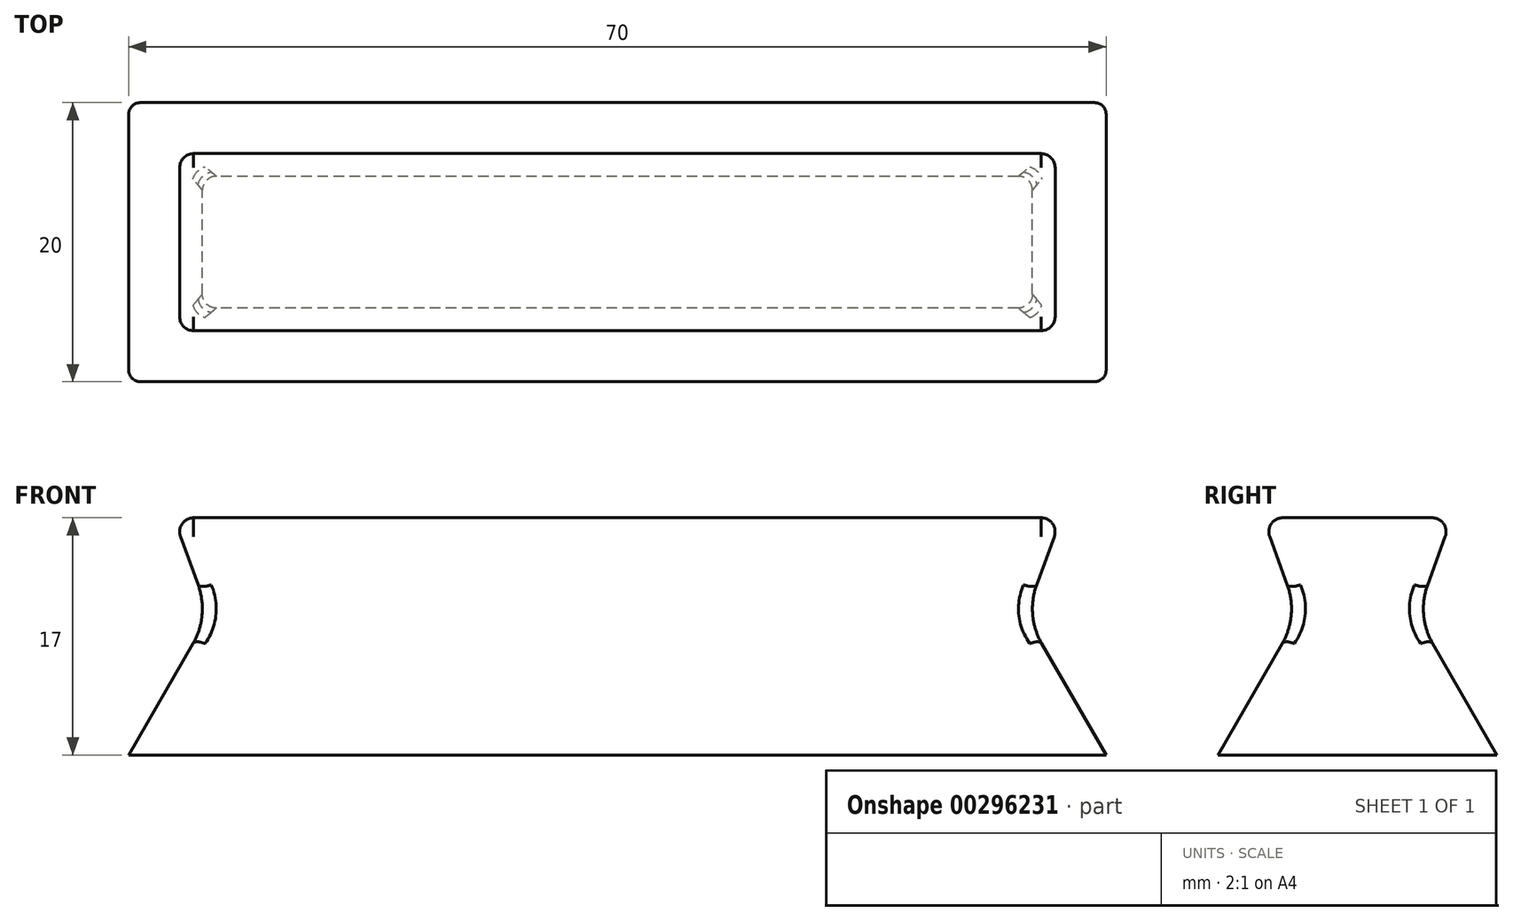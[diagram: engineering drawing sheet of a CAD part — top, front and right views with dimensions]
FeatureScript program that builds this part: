
annotation { "Feature Type Name" : "Feature", "Feature Type Description" : "" }
export const myFeature = defineFeature(function(context is Context, id is Id, definition is map)
    precondition{}
    {
        {
            var Q0;
            Q0=qCreatedBy(makeId("Top.planeOp"),FACE);
            var sketch = newSketch(context, id + "F0", { "sketchPlane" : qUnion([Q0])});
            skLineSegment(sketch, "E0.bottom", {"start": v(-35, 10) * mm, "end": v(35, 10) * mm});
            skLineSegment(sketch, "E0.top", {"start": v(-35, -10) * mm, "end": v(35, -10) * mm});
            skLineSegment(sketch, "E0.left", {"start": v(-35, 10) * mm, "end": v(-35, -10) * mm});
            skLineSegment(sketch, "E0.right", {"start": v(35, 10) * mm, "end": v(35, -10) * mm});
            skPoint(sketch, "E0.middle", {"position": v(0, 0) * mm});
            skSolve(sketch);
        }
        {
            var Q0;
            Q0=makeQuery(id+"F0.imprint","IMPRINT",FACE,{"disambiguationData":[TD([[makeQuery(id+"F0.imprint","IMPRINT",EDGE,{"derivedFrom":sQuery(id+"F0.wireOp",EDGE,"E0.bottom")}),-1.0]])]});
            extrude(context, id + "F1", {"entities" : qUnion([Q0]), "depth" : 10 * mm, "hasDraft" : true, "draftAngle" : 30 * degree, "draftPullDirection" : true});
        }
        {
            var Q0;
            Q0=makeQuery(id+"F1.opExtrude","CAP_FACE",FACE,{"disambiguationData":[OSD([sQuery(id+"F0.wireOp",EDGE,"E0.bottom"),sQuery(id+"F0.wireOp",EDGE,"E0.top"),sQuery(id+"F0.wireOp",EDGE,"E0.left"),sQuery(id+"F0.wireOp",EDGE,"E0.right")])],"isStart":false});
            extrude(context, id + "F2", {"entities" : qUnion([Q0]), "operationType" : NewBodyOperationType.ADD, "depth" : 7 * mm, "hasDraft" : true, "draftAngle" : 20 * degree});
        }
        {
            var Q0;
            {var subQ0=sQuery(id+"F0.wireOp",EDGE,"E0.top");Q0=makeQuery(id+"F2.boolean.opBoolean","MERGE",EDGE,{"derivedFrom":[makeQuery(id+"F1.opExtrude","CAP_EDGE",EDGE,{"disambiguationData":[OSD([subQ0])],"isStart":false}),makeQuery(id+"F2.opExtrude","CAP_EDGE",EDGE,{"disambiguationData":[OSD([subQ0])],"isStart":true})]});}
            fillet(context, id + "F3", {"entities" : qUnion([Q0]), "radius" : 5 * mm, "tangentPropagation" : true, "allowEdgeOverflow" : false});
        }
        {
            var Q0;
            Q0=makeQuery(id+"F2.opExtrude","CAP_EDGE",EDGE,{"disambiguationData":[OSD([sQuery(id+"F0.wireOp",EDGE,"E0.top")])],"isStart":false});
            fillet(context, id + "F4", {"entities" : qUnion([Q0]), "radius" : 1 * mm, "tangentPropagation" : true, "allowEdgeOverflow" : false});
        }
        {
            var Q0;
            {var subQ0=sQuery(id+"F0.wireOp",EDGE,"E0.bottom");Q0=makeQuery(id+"F2.boolean.opBoolean","MERGE",EDGE,{"derivedFrom":[makeQuery(id+"F1.opExtrude","CAP_EDGE",EDGE,{"disambiguationData":[OSD([subQ0])],"isStart":false}),makeQuery(id+"F2.opExtrude","CAP_EDGE",EDGE,{"disambiguationData":[OSD([subQ0])],"isStart":true})]});}
            fillet(context, id + "F5", {"entities" : qUnion([Q0]), "radius" : 5 * mm, "tangentPropagation" : true, "allowEdgeOverflow" : false});
        }
        {
            var Q0;
            Q0=makeQuery(id+"F2.opExtrude","CAP_EDGE",EDGE,{"disambiguationData":[OSD([sQuery(id+"F0.wireOp",EDGE,"E0.bottom")])],"isStart":false});
            fillet(context, id + "F6", {"entities" : qUnion([Q0]), "radius" : 1 * mm, "tangentPropagation" : true, "allowEdgeOverflow" : false});
        }
        {
            var Q0;
            {var subQ0=sQuery(id+"F0.wireOp",EDGE,"E0.right");Q0=makeQuery(id+"F2.boolean.opBoolean","MERGE",EDGE,{"derivedFrom":[makeQuery(id+"F1.opExtrude","CAP_EDGE",EDGE,{"disambiguationData":[OSD([subQ0])],"isStart":false}),makeQuery(id+"F2.opExtrude","CAP_EDGE",EDGE,{"disambiguationData":[OSD([subQ0])],"isStart":true})]});}
            fillet(context, id + "F7", {"entities" : qUnion([Q0]), "radius" : 5 * mm, "tangentPropagation" : true, "allowEdgeOverflow" : false});
        }
        {
            var Q0;
            {var subQ0=sQuery(id+"F0.wireOp",EDGE,"E0.left");Q0=makeQuery(id+"F2.boolean.opBoolean","MERGE",EDGE,{"derivedFrom":[makeQuery(id+"F1.opExtrude","CAP_EDGE",EDGE,{"disambiguationData":[OSD([subQ0])],"isStart":false}),makeQuery(id+"F2.opExtrude","CAP_EDGE",EDGE,{"disambiguationData":[OSD([subQ0])],"isStart":true})]});}
            fillet(context, id + "F8", {"entities" : qUnion([Q0]), "radius" : 5 * mm, "tangentPropagation" : true, "allowEdgeOverflow" : false});
        }
        {
            var Q0;
            Q0=makeQuery(id+"F2.opExtrude","CAP_EDGE",EDGE,{"disambiguationData":[OSD([sQuery(id+"F0.wireOp",EDGE,"E0.left")])],"isStart":false});
            fillet(context, id + "F9", {"entities" : qUnion([Q0]), "radius" : 1 * mm, "tangentPropagation" : true, "allowEdgeOverflow" : false});
        }
        {
            var Q0;
            Q0=makeQuery(id+"F2.opExtrude","CAP_EDGE",EDGE,{"disambiguationData":[OSD([sQuery(id+"F0.wireOp",EDGE,"E0.right")])],"isStart":false});
            fillet(context, id + "F10", {"entities" : qUnion([Q0]), "radius" : 1 * mm, "tangentPropagation" : true, "allowEdgeOverflow" : false});
        }
    });
